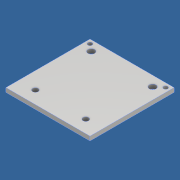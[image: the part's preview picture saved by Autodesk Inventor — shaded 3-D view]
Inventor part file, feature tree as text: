
AUTODESK INVENTOR PART (.ipt)
format: ipt  version: 2018 (Build 220112000, 112)  size: 374,272 bytes
history: native  units: mm
features: extrude x4, sketch x4, projected_geometry x1
ambient origin geometry x8: Origin, YZ Plane, XZ Plane, XY Plane, X Axis, Y Axis, Z Axis, Center Point
bodies: Solid1 (feature_tree)
feature tree (9):
  extrude  "Extrusion1"  Depth=100.0mm
  extrude  "Extrusion11"  Depth=25.0mm
  extrude  "Extrusion13"  Depth=3.3mm
  extrude  "Extrusion14"  Depth=5.0mm
  sketch  "Sketch1"  dims[d0=100.0mm d1=100.0mm]
  sketch  "Sketch7"  dims[d2=5.0mm d3=0.0mm d72=25.0mm]
  sketch  "Sketch11"  dims[d77=8.0mm d78=3.3mm]
  projected_geometry  "Projected Loop6"
  sketch  "Sketch13"  dims[d86=5.0mm d88=5.0mm d101=6.6mm d102=6.0mm d103=6.6mm d104=0.0mm d105=0.0mm d111=5.0mm d112=8.5mm d113=10.0mm d114=0.0mm d121=7.0mm d122=5.0mm d123=10.0mm d124=80.0mm d125=60.0mm d126=100.0mm d127=25.0mm d128=1.0mm d129=0.0mm]
